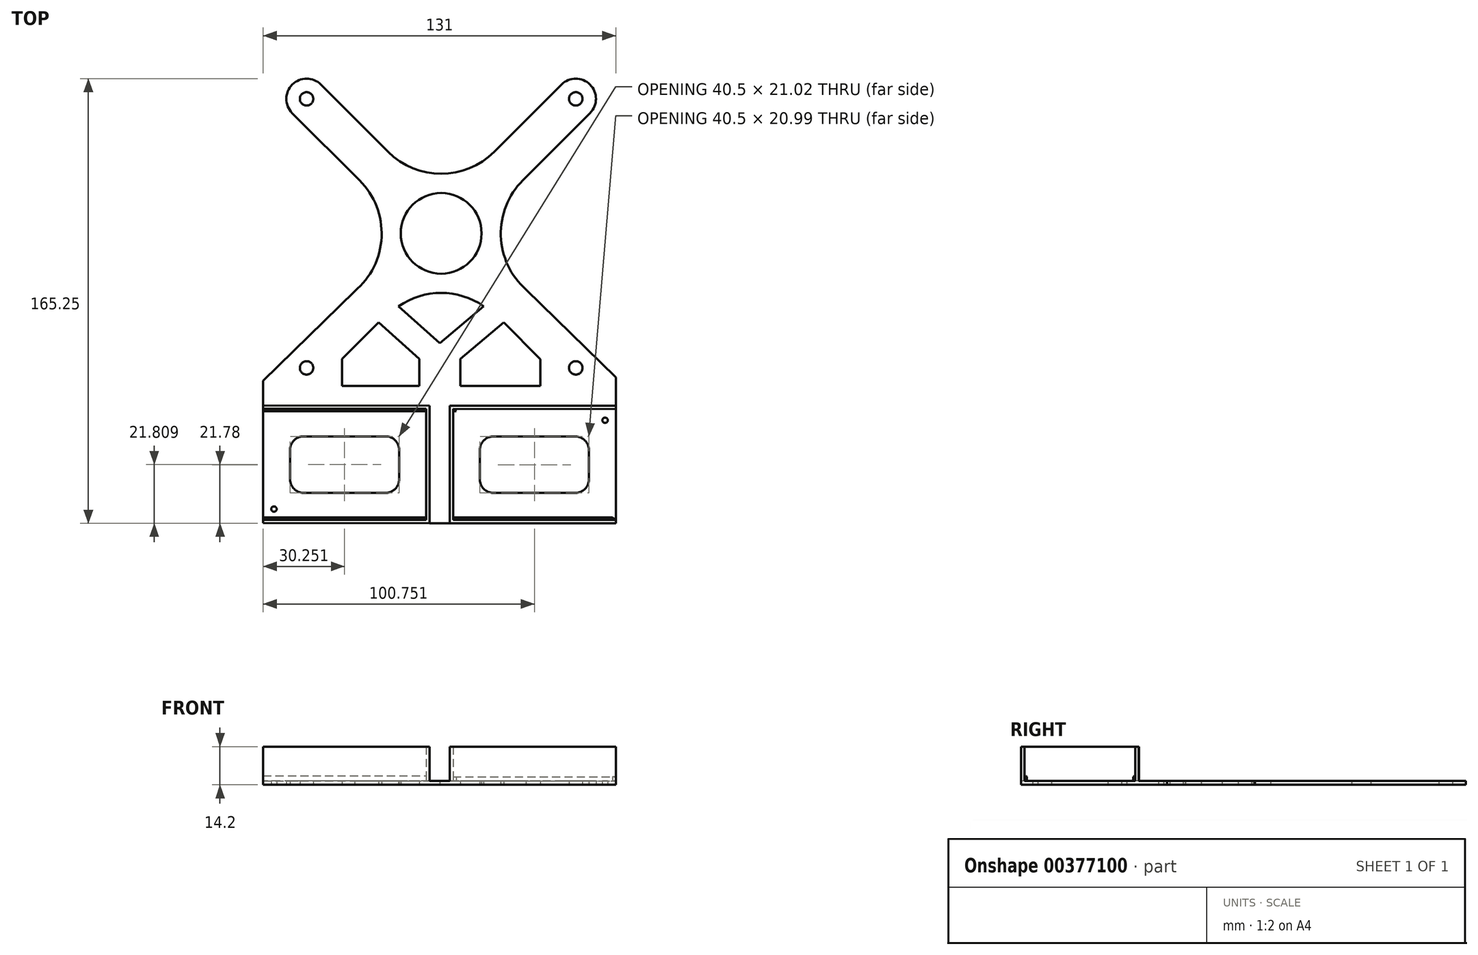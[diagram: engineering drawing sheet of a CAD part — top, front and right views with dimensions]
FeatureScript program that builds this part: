
annotation { "Feature Type Name" : "Feature", "Feature Type Description" : "" }
export const myFeature = defineFeature(function(context is Context, id is Id, definition is map)
    precondition{}
    {
        {
            var Q0;
            Q0=qCreatedBy(makeId("Top.planeOp"),FACE);
            var sketch = newSketch(context, id + "F0", { "sketchPlane" : qUnion([Q0])});
            skCircle(sketch, "E0", {"center": v(-58.44, 41.74) * mm, "radius": 2.5 * mm});
            skCircle(sketch, "E1", {"center": v(41.56, 41.74) * mm, "radius": 2.5 * mm});
            skCircle(sketch, "E2", {"center": v(41.56, -58.26) * mm, "radius": 2.5 * mm});
            skCircle(sketch, "E3", {"center": v(-58.44, -58.26) * mm, "radius": 2.5 * mm});
            skLineSegment(sketch, "E4.0", {"start": v(-28.13, 22.05) * mm, "end": v(-53.13, 47.05) * mm});
            skArc(sketch, "E5.0", {"start": v(-53.13, 47.05) * mm, "mid": v(-63.74, 47.05) * mm, "end": v(-63.74, 36.44) * mm});
            skLineSegment(sketch, "E6.0", {"start": v(-38.74, 11.44) * mm, "end": v(-63.74, 36.44) * mm});
            skArc(sketch, "E7.0", {"start": v(-38.74, 11.44) * mm, "mid": v(-30.58, -9.59) * mm, "end": v(-40.6, -29.8) * mm});
            skLineSegment(sketch, "E8.0", {"start": v(-31.66, -41.35) * mm, "end": v(-45.26, -54.95) * mm});
            skArc(sketch, "E9.0", {"start": v(7.36, -35.31) * mm, "mid": v(-8.45, -30.4) * mm, "end": v(-24.25, -35.33) * mm});
            skLineSegment(sketch, "E10.0", {"start": v(28.45, -55) * mm, "end": v(14.82, -41.36) * mm});
            skArc(sketch, "E11.0", {"start": v(21.87, 11.44) * mm, "mid": v(13.7, -9.12) * mm, "end": v(23.09, -29.16) * mm});
            skLineSegment(sketch, "E12.0", {"start": v(21.87, 11.44) * mm, "end": v(46.87, 36.44) * mm});
            skArc(sketch, "E13.0", {"start": v(46.87, 36.44) * mm, "mid": v(46.87, 47.05) * mm, "end": v(36.26, 47.05) * mm});
            skLineSegment(sketch, "E14.0", {"start": v(11.26, 22.05) * mm, "end": v(36.26, 47.05) * mm});
            skArc(sketch, "E15.0", {"start": v(-28.13, 22.05) * mm, "mid": v(-8.44, 13.89) * mm, "end": v(11.26, 22.05) * mm});
            skCircle(sketch, "E16", {"center": v(-8.44, -8.26) * mm, "radius": 15 * mm});
            skLineSegment(sketch, "E17.0", {"start": v(-1.3, -54.98) * mm, "end": v(14.82, -41.36) * mm});
            skLineSegment(sketch, "E18.0", {"start": v(-8.96, -49.09) * mm, "end": v(7.36, -35.31) * mm});
            skLineSegment(sketch, "E19.0", {"start": v(-31.66, -41.35) * mm, "end": v(-16.53, -54.97) * mm});
            skLineSegment(sketch, "E20.0", {"start": v(-24.25, -35.33) * mm, "end": v(-8.96, -49.09) * mm});
            skPoint(sketch, "E21.orphan", {"position": v(-59.42, -54.94) * mm});
            skLineSegment(sketch, "E22.0", {"start": v(-4.06, -64.97) * mm, "end": v(-4.06, -64.98) * mm});
            skLineSegment(sketch, "E23.0", {"start": v(56.44, -61.77) * mm, "end": v(56.44, -116.01) * mm});
            skLineSegment(sketch, "E24.0", {"start": v(-74.56, -114.68) * mm, "end": v(-74.56, -115.93) * mm});
            skLineSegment(sketch, "E25.0", {"start": v(56.44, -116.01) * mm, "end": v(-74.56, -115.93) * mm});
            skLineSegment(sketch, "E26.0", {"start": v(-5.3, -64.97) * mm, "end": v(-5.3, -64.98) * mm});
            skLineSegment(sketch, "E27.0", {"start": v(32, -51.46) * mm, "end": v(18.35, -37.82) * mm});
            skLineSegment(sketch, "E28", {"start": v(23.09, -29.16) * mm, "end": v(56.44, -61.77) * mm});
            skLineSegment(sketch, "E29", {"start": v(-40.6, -29.8) * mm, "end": v(-74.56, -63.04) * mm});
            skLineSegment(sketch, "E30.0", {"start": v(10.94, -104.73) * mm, "end": v(41.44, -104.73) * mm});
            skLineSegment(sketch, "E31.0", {"start": v(5.94, -88.73) * mm, "end": v(5.94, -99.73) * mm});
            skLineSegment(sketch, "E32.0", {"start": v(41.44, -83.75) * mm, "end": v(10.94, -83.73) * mm});
            skLineSegment(sketch, "E33.0", {"start": v(46.44, -88.75) * mm, "end": v(46.44, -99.73) * mm});
            skArc(sketch, "E34.filletArc", {"start": v(46.44, -88.75) * mm, "mid": v(44.98, -85.22) * mm, "end": v(41.44, -83.75) * mm});
            skArc(sketch, "E35.filletArc", {"start": v(41.44, -104.73) * mm, "mid": v(44.98, -103.26) * mm, "end": v(46.44, -99.73) * mm});
            skArc(sketch, "E36.filletArc", {"start": v(5.94, -99.73) * mm, "mid": v(7.4, -103.26) * mm, "end": v(10.94, -104.73) * mm});
            skArc(sketch, "E37.filletArc", {"start": v(10.94, -83.73) * mm, "mid": v(7.4, -85.2) * mm, "end": v(5.94, -88.73) * mm});
            skLineSegment(sketch, "E38", {"start": v(28.45, -55) * mm, "end": v(28.45, -65) * mm});
            skLineSegment(sketch, "E39", {"start": v(28.45, -65) * mm, "end": v(-1.3, -65) * mm});
            skLineSegment(sketch, "E40", {"start": v(-1.3, -65) * mm, "end": v(-1.3, -54.98) * mm});
            skLineSegment(sketch, "E41", {"start": v(-16.53, -54.97) * mm, "end": v(-16.53, -64.97) * mm});
            skLineSegment(sketch, "E42", {"start": v(-16.53, -64.97) * mm, "end": v(-45.26, -64.97) * mm});
            skLineSegment(sketch, "E43", {"start": v(-45.26, -64.97) * mm, "end": v(-45.26, -54.95) * mm});
            skLineSegment(sketch, "E44.0", {"start": v(-24.06, -88.71) * mm, "end": v(-24.06, -99.71) * mm});
            skLineSegment(sketch, "E45.0", {"start": v(-29.06, -83.71) * mm, "end": v(-59.56, -83.7) * mm});
            skLineSegment(sketch, "E46.0", {"start": v(-64.56, -88.7) * mm, "end": v(-64.56, -99.7) * mm});
            skLineSegment(sketch, "E47.0", {"start": v(-29.06, -104.71) * mm, "end": v(-59.56, -104.7) * mm});
            skArc(sketch, "E48.filletArc", {"start": v(-24.06, -88.71) * mm, "mid": v(-25.52, -85.18) * mm, "end": v(-29.06, -83.71) * mm});
            skArc(sketch, "E49.filletArc", {"start": v(-29.06, -104.71) * mm, "mid": v(-25.53, -103.25) * mm, "end": v(-24.06, -99.71) * mm});
            skArc(sketch, "E50.filletArc", {"start": v(-64.56, -99.7) * mm, "mid": v(-63.1, -103.23) * mm, "end": v(-59.56, -104.7) * mm});
            skArc(sketch, "E51.filletArc", {"start": v(-59.56, -83.7) * mm, "mid": v(-63.1, -85.16) * mm, "end": v(-64.56, -88.7) * mm});
            skLineSegment(sketch, "E52", {"start": v(-74.56, -63.04) * mm, "end": v(-74.53, -72.43) * mm});
            skLineSegment(sketch, "E53", {"start": v(-74.53, -72.43) * mm, "end": v(-74.53, -73.68) * mm});
            skLineSegment(sketch, "E54", {"start": v(-74.53, -73.68) * mm, "end": v(-74.56, -114.68) * mm});
            skCircle(sketch, "E55", {"center": v(-70.56, -110.73) * mm, "radius": 1 * mm});
            skCircle(sketch, "E56", {"center": v(52.44, -77.72) * mm, "radius": 1 * mm});
            skSolve(sketch);
        }
        {
            var Q0;
            Q0=makeQuery(id+"F0.imprint","IMPRINT",FACE,{"disambiguationData":[TD([[makeQuery(id+"F0.imprint","IMPRINT",EDGE,{"derivedFrom":sQuery(id+"F0.wireOp",EDGE,"E0")}),-1.0]])]});
            extrude(context, id + "F1", {"entities" : qUnion([Q0]), "depth" : 1.5 * mm});
        }
        {
            var Q0;
            Q0=makeQuery(id+"F1.opExtrude","CAP_FACE",FACE,{"disambiguationData":[OSD([sQuery(id+"F0.wireOp",EDGE,"E0"),sQuery(id+"F0.wireOp",EDGE,"E1"),sQuery(id+"F0.wireOp",EDGE,"E2"),sQuery(id+"F0.wireOp",EDGE,"E3"),sQuery(id+"F0.wireOp",EDGE,"E4.0"),sQuery(id+"F0.wireOp",EDGE,"E5.0"),sQuery(id+"F0.wireOp",EDGE,"E6.0"),sQuery(id+"F0.wireOp",EDGE,"E7.0"),sQuery(id+"F0.wireOp",EDGE,"E8.0"),sQuery(id+"F0.wireOp",EDGE,"E9.0"),sQuery(id+"F0.wireOp",EDGE,"E10.0"),sQuery(id+"F0.wireOp",EDGE,"E11.0"),sQuery(id+"F0.wireOp",EDGE,"E12.0"),sQuery(id+"F0.wireOp",EDGE,"E13.0"),sQuery(id+"F0.wireOp",EDGE,"E14.0"),sQuery(id+"F0.wireOp",EDGE,"E15.0"),sQuery(id+"F0.wireOp",EDGE,"E16"),sQuery(id+"F0.wireOp",EDGE,"E17.0"),sQuery(id+"F0.wireOp",EDGE,"E18.0"),sQuery(id+"F0.wireOp",EDGE,"E19.0"),sQuery(id+"F0.wireOp",EDGE,"E20.0"),sQuery(id+"F0.wireOp",EDGE,"E23.0"),sQuery(id+"F0.wireOp",EDGE,"E24.0"),sQuery(id+"F0.wireOp",EDGE,"E25.0"),sQuery(id+"F0.wireOp",EDGE,"vcMs6dal-6m1P-AOfd-6HBZ-Wd8BayPtVPf2"),sQuery(id+"F0.wireOp",EDGE,"bRpbFbSv-FE7c-4cWb-KfAA-hbhdmxlXRJBx"),sQuery(id+"F0.wireOp",EDGE,"E28"),sQuery(id+"F0.wireOp",EDGE,"E29"),sQuery(id+"F0.wireOp",EDGE,"E30.0"),sQuery(id+"F0.wireOp",EDGE,"E31.0"),sQuery(id+"F0.wireOp",EDGE,"E32.0"),sQuery(id+"F0.wireOp",EDGE,"E33.0"),sQuery(id+"F0.wireOp",EDGE,"E34.filletArc"),sQuery(id+"F0.wireOp",EDGE,"E35.filletArc"),sQuery(id+"F0.wireOp",EDGE,"E36.filletArc"),sQuery(id+"F0.wireOp",EDGE,"E37.filletArc"),sQuery(id+"F0.wireOp",EDGE,"E38"),sQuery(id+"F0.wireOp",EDGE,"E39"),sQuery(id+"F0.wireOp",EDGE,"E40"),sQuery(id+"F0.wireOp",EDGE,"E41"),sQuery(id+"F0.wireOp",EDGE,"E42"),sQuery(id+"F0.wireOp",EDGE,"E43"),sQuery(id+"F0.wireOp",EDGE,"E44.0"),sQuery(id+"F0.wireOp",EDGE,"E45.0"),sQuery(id+"F0.wireOp",EDGE,"E46.0"),sQuery(id+"F0.wireOp",EDGE,"E47.0"),sQuery(id+"F0.wireOp",EDGE,"E48.filletArc"),sQuery(id+"F0.wireOp",EDGE,"E49.filletArc"),sQuery(id+"F0.wireOp",EDGE,"E50.filletArc"),sQuery(id+"F0.wireOp",EDGE,"E51.filletArc"),sQuery(id+"F0.wireOp",EDGE,"E52"),sQuery(id+"F0.wireOp",EDGE,"E53"),sQuery(id+"F0.wireOp",EDGE,"E54")])],"isStart":false});
            var sketch = newSketch(context, id + "F2", { "sketchPlane" : qUnion([Q0])});
            skLineSegment(sketch, "E57", {"start": v(-74.56, -115.93) * mm, "end": v(56.44, -116.01) * mm});
            skLineSegment(sketch, "E58.0", {"start": v(-74.56, -114.68) * mm, "end": v(-14.03, -114.72) * mm});
            skLineSegment(sketch, "E59.0", {"start": v(-74.53, -73.68) * mm, "end": v(-14.03, -73.72) * mm});
            skLineSegment(sketch, "E60", {"start": v(56.47, -72.31) * mm, "end": v(56.47, -73.76) * mm});
            skLineSegment(sketch, "E61", {"start": v(-74.53, -72.23) * mm, "end": v(-74.53, -73.68) * mm});
            skLineSegment(sketch, "E62", {"start": v(-74.56, -114.68) * mm, "end": v(-74.56, -115.93) * mm});
            skLineSegment(sketch, "E63", {"start": v(56.44, -114.76) * mm, "end": v(56.44, -116.01) * mm});
            skLineSegment(sketch, "E64.0", {"start": v(-14.03, -73.52) * mm, "end": v(-14.03, -114.72) * mm});
            skLineSegment(sketch, "E65.0", {"start": v(-4.03, -73.53) * mm, "end": v(-4.03, -114.73) * mm});
            skLineSegment(sketch, "E66.0", {"start": v(-5.28, -72.28) * mm, "end": v(-5.28, -115.98) * mm});
            skLineSegment(sketch, "E67.0", {"start": v(-12.78, -72.27) * mm, "end": v(-12.78, -115.97) * mm});
            skLineSegment(sketch, "E68.trimOffspring", {"start": v(-4.03, -73.73) * mm, "end": v(56.47, -73.76) * mm});
            skLineSegment(sketch, "E69.trimOffspring", {"start": v(-12.78, -114.72) * mm, "end": v(-5.28, -114.73) * mm});
            skLineSegment(sketch, "E70.trimOffspring", {"start": v(-4.03, -114.73) * mm, "end": v(56.44, -114.76) * mm});
            skLineSegment(sketch, "E71.0", {"start": v(-74.53, -73.48) * mm, "end": v(-14.03, -73.52) * mm});
            skLineSegment(sketch, "E72.0", {"start": v(-74.53, -72.23) * mm, "end": v(-12.78, -72.27) * mm});
            skLineSegment(sketch, "E73.0", {"start": v(-5.28, -72.28) * mm, "end": v(56.47, -72.31) * mm});
            skLineSegment(sketch, "E74.0", {"start": v(-4.03, -73.53) * mm, "end": v(56.47, -73.56) * mm});
            skSolve(sketch);
        }
        {
            var Q0;
            {var subQ6=sQuery(id+"F2.wireOp",EDGE,"E70.trimOffspring");var subQ7=sQuery(id+"F2.wireOp",EDGE,"E65.0");var subQ8=makeQuery(id+"F2.imprint","INTERSECT",VERTEX,{"derivedFrom":[subQ7,subQ6]});Q0=makeQuery(id+"F2.imprint","IMPRINT",FACE,{"disambiguationData":[TD([[makeQuery(id+"F2.imprint","IMPRINT",EDGE,{"disambiguationData":[TD([[subQ8,1.0]])],"derivedFrom":subQ7}),-1.0]])]});}
            var Q1;
            {var subQ6=sQuery(id+"F2.wireOp",EDGE,"E58.0");Q1=makeQuery(id+"F2.imprint","IMPRINT",FACE,{"disambiguationData":[TD([[makeQuery(id+"F2.imprint","IMPRINT",EDGE,{"derivedFrom":subQ6}),-1.0]])]});}
            extrude(context, id + "F3", {"entities" : qUnion([Q0, Q1]), "operationType" : NewBodyOperationType.ADD, "depth" : 12.7 * mm});
        }
        {
            var Q0;
            {var subQ0=sQuery(id+"F0.wireOp",EDGE,"E53");var subQ1=sQuery(id+"F0.wireOp",EDGE,"E51.filletArc");var subQ2=sQuery(id+"F0.wireOp",EDGE,"E50.filletArc");var subQ3=sQuery(id+"F0.wireOp",EDGE,"E49.filletArc");var subQ4=sQuery(id+"F0.wireOp",EDGE,"E24.0");var subQ5=sQuery(id+"F0.wireOp",EDGE,"E47.0");var subQ6=sQuery(id+"F0.wireOp",EDGE,"E48.filletArc");var subQ7=sQuery(id+"F0.wireOp",EDGE,"E46.0");var subQ8=sQuery(id+"F0.wireOp",EDGE,"E44.0");var subQ9=sQuery(id+"F0.wireOp",EDGE,"E45.0");var subQ10=sQuery(id+"F0.wireOp",EDGE,"E54");var subQ11=sQuery(id+"F0.wireOp",EDGE,"E55");Q0=makeQuery(id+"F3.boolean.opBoolean","SPLIT",FACE,{"disambiguationData":[TD([makeQuery(id+"F1.opExtrude","SWEPT_FACE",FACE,{"disambiguationData":[OSD([subQ4])]})])],"derivedFrom":makeQuery(id+"F1.opExtrude","CAP_FACE",FACE,{"disambiguationData":[OSD([sQuery(id+"F0.wireOp",EDGE,"E0"),sQuery(id+"F0.wireOp",EDGE,"E1"),sQuery(id+"F0.wireOp",EDGE,"E2"),sQuery(id+"F0.wireOp",EDGE,"E3"),sQuery(id+"F0.wireOp",EDGE,"E4.0"),sQuery(id+"F0.wireOp",EDGE,"E5.0"),sQuery(id+"F0.wireOp",EDGE,"E6.0"),sQuery(id+"F0.wireOp",EDGE,"E7.0"),sQuery(id+"F0.wireOp",EDGE,"E8.0"),sQuery(id+"F0.wireOp",EDGE,"E9.0"),sQuery(id+"F0.wireOp",EDGE,"E10.0"),sQuery(id+"F0.wireOp",EDGE,"E11.0"),sQuery(id+"F0.wireOp",EDGE,"E12.0"),sQuery(id+"F0.wireOp",EDGE,"E13.0"),sQuery(id+"F0.wireOp",EDGE,"E14.0"),sQuery(id+"F0.wireOp",EDGE,"E15.0"),sQuery(id+"F0.wireOp",EDGE,"E16"),sQuery(id+"F0.wireOp",EDGE,"E17.0"),sQuery(id+"F0.wireOp",EDGE,"E18.0"),sQuery(id+"F0.wireOp",EDGE,"E19.0"),sQuery(id+"F0.wireOp",EDGE,"E20.0"),sQuery(id+"F0.wireOp",EDGE,"E23.0"),subQ4,sQuery(id+"F0.wireOp",EDGE,"E25.0"),sQuery(id+"F0.wireOp",EDGE,"E28"),sQuery(id+"F0.wireOp",EDGE,"E29"),sQuery(id+"F0.wireOp",EDGE,"E30.0"),sQuery(id+"F0.wireOp",EDGE,"E31.0"),sQuery(id+"F0.wireOp",EDGE,"E32.0"),sQuery(id+"F0.wireOp",EDGE,"E33.0"),sQuery(id+"F0.wireOp",EDGE,"E34.filletArc"),sQuery(id+"F0.wireOp",EDGE,"E35.filletArc"),sQuery(id+"F0.wireOp",EDGE,"E36.filletArc"),sQuery(id+"F0.wireOp",EDGE,"E37.filletArc"),sQuery(id+"F0.wireOp",EDGE,"E38"),sQuery(id+"F0.wireOp",EDGE,"E39"),sQuery(id+"F0.wireOp",EDGE,"E40"),sQuery(id+"F0.wireOp",EDGE,"E41"),sQuery(id+"F0.wireOp",EDGE,"E42"),sQuery(id+"F0.wireOp",EDGE,"E43"),subQ8,subQ9,subQ7,subQ5,subQ6,subQ3,subQ2,subQ1,sQuery(id+"F0.wireOp",EDGE,"E52"),subQ0,subQ10,subQ11,sQuery(id+"F0.wireOp",EDGE,"E56")])],"isStart":false})});}
            var sketch = newSketch(context, id + "F4", { "sketchPlane" : qUnion([Q0])});
            skLineSegment(sketch, "E75", {"start": v(-14.03, -114.72) * mm, "end": v(-14.03, -115.54) * mm});
            skLineSegment(sketch, "E76", {"start": v(-74.56, -114.68) * mm, "end": v(-74.56, -113.86) * mm});
            skLineSegment(sketch, "E77", {"start": v(-74.56, -113.86) * mm, "end": v(-14.03, -113.9) * mm});
            skLineSegment(sketch, "E78", {"start": v(-14.03, -113.9) * mm, "end": v(-14.03, -114.72) * mm});
            skLineSegment(sketch, "E79", {"start": v(-74.53, -73.48) * mm, "end": v(-74.53, -74.3) * mm});
            skLineSegment(sketch, "E80", {"start": v(-74.53, -74.3) * mm, "end": v(-14.03, -74.34) * mm});
            skLineSegment(sketch, "E81", {"start": v(-14.03, -74.34) * mm, "end": v(-14.03, -73.52) * mm});
            skLineSegment(sketch, "E82", {"start": v(-14.03, -73.52) * mm, "end": v(-74.53, -73.48) * mm});
            skLineSegment(sketch, "E83", {"start": v(-74.56, -113.86) * mm, "end": v(-74.56, -114.68) * mm});
            skLineSegment(sketch, "E84", {"start": v(-74.56, -114.68) * mm, "end": v(-14.03, -114.72) * mm});
            skSolve(sketch);
        }
        {
            var Q0;
            {var subQ0=sQuery(id+"F0.wireOp",EDGE,"E37.filletArc");var subQ1=sQuery(id+"F0.wireOp",EDGE,"E35.filletArc");var subQ2=sQuery(id+"F0.wireOp",EDGE,"E56");var subQ3=sQuery(id+"F0.wireOp",EDGE,"E33.0");var subQ4=sQuery(id+"F0.wireOp",EDGE,"E34.filletArc");var subQ5=sQuery(id+"F0.wireOp",EDGE,"E36.filletArc");var subQ6=sQuery(id+"F0.wireOp",EDGE,"E23.0");var subQ9=sQuery(id+"F0.wireOp",EDGE,"E30.0");var subQ10=sQuery(id+"F0.wireOp",EDGE,"E31.0");var subQ11=sQuery(id+"F0.wireOp",EDGE,"E32.0");Q0=makeQuery(id+"F3.boolean.opBoolean","SPLIT",FACE,{"disambiguationData":[TD([makeQuery(id+"F1.opExtrude","SWEPT_FACE",FACE,{"disambiguationData":[OSD([subQ9])]})])],"derivedFrom":makeQuery(id+"F1.opExtrude","CAP_FACE",FACE,{"disambiguationData":[OSD([sQuery(id+"F0.wireOp",EDGE,"E0"),sQuery(id+"F0.wireOp",EDGE,"E1"),sQuery(id+"F0.wireOp",EDGE,"E2"),sQuery(id+"F0.wireOp",EDGE,"E3"),sQuery(id+"F0.wireOp",EDGE,"E4.0"),sQuery(id+"F0.wireOp",EDGE,"E5.0"),sQuery(id+"F0.wireOp",EDGE,"E6.0"),sQuery(id+"F0.wireOp",EDGE,"E7.0"),sQuery(id+"F0.wireOp",EDGE,"E8.0"),sQuery(id+"F0.wireOp",EDGE,"E9.0"),sQuery(id+"F0.wireOp",EDGE,"E10.0"),sQuery(id+"F0.wireOp",EDGE,"E11.0"),sQuery(id+"F0.wireOp",EDGE,"E12.0"),sQuery(id+"F0.wireOp",EDGE,"E13.0"),sQuery(id+"F0.wireOp",EDGE,"E14.0"),sQuery(id+"F0.wireOp",EDGE,"E15.0"),sQuery(id+"F0.wireOp",EDGE,"E16"),sQuery(id+"F0.wireOp",EDGE,"E17.0"),sQuery(id+"F0.wireOp",EDGE,"E18.0"),sQuery(id+"F0.wireOp",EDGE,"E19.0"),sQuery(id+"F0.wireOp",EDGE,"E20.0"),subQ6,sQuery(id+"F0.wireOp",EDGE,"E24.0"),sQuery(id+"F0.wireOp",EDGE,"E25.0"),sQuery(id+"F0.wireOp",EDGE,"E28"),sQuery(id+"F0.wireOp",EDGE,"E29"),subQ9,subQ10,subQ11,subQ3,subQ4,subQ1,subQ5,subQ0,sQuery(id+"F0.wireOp",EDGE,"E38"),sQuery(id+"F0.wireOp",EDGE,"E39"),sQuery(id+"F0.wireOp",EDGE,"E40"),sQuery(id+"F0.wireOp",EDGE,"E41"),sQuery(id+"F0.wireOp",EDGE,"E42"),sQuery(id+"F0.wireOp",EDGE,"E43"),sQuery(id+"F0.wireOp",EDGE,"E44.0"),sQuery(id+"F0.wireOp",EDGE,"E45.0"),sQuery(id+"F0.wireOp",EDGE,"E46.0"),sQuery(id+"F0.wireOp",EDGE,"E47.0"),sQuery(id+"F0.wireOp",EDGE,"E48.filletArc"),sQuery(id+"F0.wireOp",EDGE,"E49.filletArc"),sQuery(id+"F0.wireOp",EDGE,"E50.filletArc"),sQuery(id+"F0.wireOp",EDGE,"E51.filletArc"),sQuery(id+"F0.wireOp",EDGE,"E52"),sQuery(id+"F0.wireOp",EDGE,"E53"),sQuery(id+"F0.wireOp",EDGE,"E54"),sQuery(id+"F0.wireOp",EDGE,"E55"),subQ2])],"isStart":false})});}
            var sketch = newSketch(context, id + "F5", { "sketchPlane" : qUnion([Q0])});
            skLineSegment(sketch, "E85", {"start": v(-4.03, -73.53) * mm, "end": v(-4.03, -74.35) * mm});
            skLineSegment(sketch, "E86", {"start": v(56.44, -74.35) * mm, "end": v(56.44, -114.76) * mm});
            skLineSegment(sketch, "E87", {"start": v(56.44, -114.76) * mm, "end": v(-4.03, -73.53) * mm});
            skLineSegment(sketch, "E88", {"start": v(-4.03, -114.73) * mm, "end": v(-4.03, -113.9) * mm});
            skLineSegment(sketch, "E89", {"start": v(-4.03, -113.9) * mm, "end": v(56.44, -113.9) * mm});
            skLineSegment(sketch, "E90", {"start": v(56.44, -113.9) * mm, "end": v(56.44, -114.76) * mm});
            skLineSegment(sketch, "E91", {"start": v(56.44, -114.76) * mm, "end": v(-4.03, -114.73) * mm});
            skLineSegment(sketch, "E92", {"start": v(-4.03, -74.35) * mm, "end": v(56.44, -74.35) * mm});
            skLineSegment(sketch, "E93", {"start": v(56.44, -73.56) * mm, "end": v(-4.03, -73.53) * mm});
            skSolve(sketch);
        }
        {
            var Q0;
            Q0=makeQuery(id+"F5.imprint","IMPRINT",FACE,{"disambiguationData":[TD([[makeQuery(id+"F5.imprint","IMPRINT",EDGE,{"derivedFrom":sQuery(id+"F5.wireOp",EDGE,"E88")}),1.0]])]});
            var Q1;
            Q1=makeQuery(id+"F5.imprint","IMPRINT",FACE,{"disambiguationData":[TD([[makeQuery(id+"F5.imprint","IMPRINT",EDGE,{"derivedFrom":sQuery(id+"F5.wireOp",EDGE,"E85")}),1.0]])]});
            extrude(context, id + "F6", {"entities" : qUnion([Q0, Q1]), "operationType" : NewBodyOperationType.ADD, "depth" : 1.5 * mm});
        }
        {
            var Q0;
            Q0=makeQuery(id+"F4.imprint","IMPRINT",FACE,{"disambiguationData":[TD([[makeQuery(id+"F4.imprint","IMPRINT",EDGE,{"derivedFrom":sQuery(id+"F4.wireOp",EDGE,"E77")}),-1.0]])]});
            var Q1;
            {var subQ0=sQuery(id+"F4.wireOp",EDGE,"E80");Q1=makeQuery(id+"F4.imprint","IMPRINT",FACE,{"disambiguationData":[TD([[makeQuery(id+"F4.imprint","IMPRINT",EDGE,{"derivedFrom":subQ0}),1.0]])]});}
            extrude(context, id + "F7", {"entities" : qUnion([Q0, Q1]), "operationType" : NewBodyOperationType.ADD, "depth" : 1.8 * mm});
        }
    });
